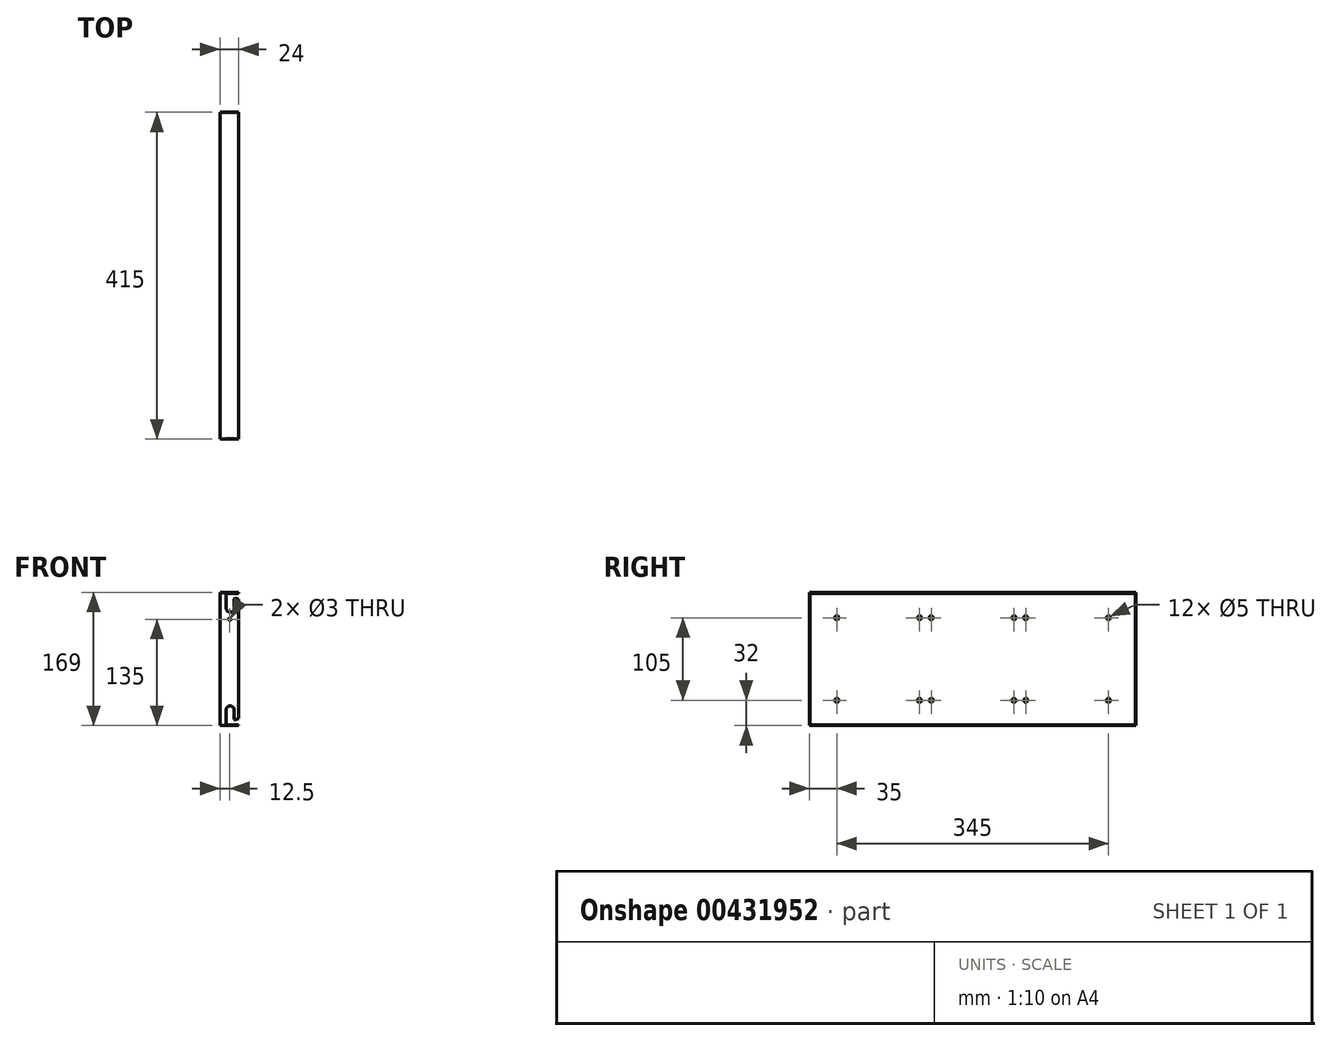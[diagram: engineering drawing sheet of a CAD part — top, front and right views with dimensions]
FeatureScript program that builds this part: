
annotation { "Feature Type Name" : "Feature", "Feature Type Description" : "" }
export const myFeature = defineFeature(function(context is Context, id is Id, definition is map)
    precondition{}
    {
        {
            var Q0;
            Q0=qCreatedBy(makeId("Right.planeOp"),FACE);
            var sketch = newSketch(context, id + "F0", { "sketchPlane" : qUnion([Q0])});
            skLineSegment(sketch, "E0.bottom", {"start": v(-207.5, 84.5) * mm, "end": v(207.5, 84.5) * mm});
            skLineSegment(sketch, "E0.top", {"start": v(-207.5, -84.5) * mm, "end": v(207.5, -84.5) * mm});
            skLineSegment(sketch, "E0.left", {"start": v(-207.5, 84.5) * mm, "end": v(-207.5, -84.5) * mm});
            skLineSegment(sketch, "E0.right", {"start": v(207.5, 84.5) * mm, "end": v(207.5, -84.5) * mm});
            skPoint(sketch, "E0.middle", {"position": v(0, 0) * mm});
            skSolve(sketch);
        }
        {
            var Q0;
            Q0 = qSketchRegion(id + "F0", true);
            extrude(context, id + "F1", {"entities" : qUnion([Q0]), "depth" : 24 * mm});
        }
        {
            var Q0;
            Q0=makeQuery(id+"F1.opExtrude","CAP_FACE",FACE,{"disambiguationData":[OSD([sQuery(id+"F0.wireOp",EDGE,"E0.bottom"),sQuery(id+"F0.wireOp",EDGE,"E0.top"),sQuery(id+"F0.wireOp",EDGE,"E0.left"),sQuery(id+"F0.wireOp",EDGE,"E0.right")])],"isStart":false});
            var sketch = newSketch(context, id + "F2", { "sketchPlane" : qUnion([Q0])});
            skLineSegment(sketch, "E1.bottom", {"start": v(-206.5, 83.5) * mm, "end": v(206.5, 83.5) * mm});
            skLineSegment(sketch, "E1.top", {"start": v(-206.5, -83.5) * mm, "end": v(206.5, -83.5) * mm});
            skLineSegment(sketch, "E1.left", {"start": v(-206.5, 83.5) * mm, "end": v(-206.5, -83.5) * mm});
            skLineSegment(sketch, "E1.right", {"start": v(206.5, 83.5) * mm, "end": v(206.5, -83.5) * mm});
            skPoint(sketch, "E1.middle", {"position": v(0, 0) * mm});
            skSolve(sketch);
        }
        {
            var Q0;
            Q0 = qSketchRegion(id + "F2", true);
            extrude(context, id + "F3", {"entities" : qUnion([Q0]), "operationType" : NewBodyOperationType.REMOVE, "oppositeDirection" : true, "depth" : 23 * mm});
        }
        {
            var Q0;
            Q0=makeQuery(id+"F1.opExtrude","SWEPT_FACE",FACE,{"disambiguationData":[OSD([sQuery(id+"F0.wireOp",EDGE,"E0.left")])]});
            var sketch = newSketch(context, id + "F4", { "sketchPlane" : qUnion([Q0])});
            skLineSegment(sketch, "E2", {"start": v(24, -83.5) * mm, "end": v(8, -83.5) * mm});
            skLineSegment(sketch, "E3", {"start": v(8, -83.5) * mm, "end": v(8, -64.5) * mm});
            skLineSegment(sketch, "E4", {"start": v(18, -76.5) * mm, "end": v(18, -64.5) * mm});
            skLineSegment(sketch, "E5", {"start": v(18, -64.5) * mm, "end": v(8, -64.5) * mm, "construction": true});
            skArc(sketch, "E6", {"start": v(8, -64.5) * mm, "mid": v(13, -59.5) * mm, "end": v(18, -64.5) * mm});
            skLineSegment(sketch, "E7", {"start": v(18, -76.5) * mm, "end": v(19.5, -77.5) * mm});
            skLineSegment(sketch, "E8", {"start": v(24, -75.5) * mm, "end": v(24, -83.5) * mm});
            skLineSegment(sketch, "E9", {"start": v(19.5, -77.5) * mm, "end": v(24, -75.5) * mm});
            skLineSegment(sketch, "E10", {"start": v(0, 0) * mm, "end": v(24, 0) * mm, "construction": true});
            skLineSegment(sketch, "E11.MirrorCS", {"start": v(18, 76.5) * mm, "end": v(19.5, 77.5) * mm});
            skLineSegment(sketch, "E12.MirrorCS", {"start": v(24, 75.5) * mm, "end": v(24, 83.5) * mm});
            skLineSegment(sketch, "E13.MirrorCS", {"start": v(19.5, 77.5) * mm, "end": v(24, 75.5) * mm});
            skLineSegment(sketch, "E14.MirrorCS", {"start": v(18, 64.5) * mm, "end": v(8, 64.5) * mm, "construction": true});
            skLineSegment(sketch, "E15.MirrorCS", {"start": v(18, 76.5) * mm, "end": v(18, 64.5) * mm});
            skArc(sketch, "E16.MirrorCS", {"start": v(8, 64.5) * mm, "mid": v(13, 59.5) * mm, "end": v(18, 64.5) * mm});
            skLineSegment(sketch, "E17.MirrorCS", {"start": v(24, 83.5) * mm, "end": v(8, 83.5) * mm});
            skLineSegment(sketch, "E18.MirrorCS", {"start": v(8, 83.5) * mm, "end": v(8, 64.5) * mm});
            skSolve(sketch);
        }
        {
            var Q0;
            Q0 = qSketchRegion(id + "F4", true);
            extrude(context, id + "F5", {"entities" : qUnion([Q0]), "operationType" : NewBodyOperationType.REMOVE, "endBound" : BoundingType.THROUGH_ALL, "oppositeDirection" : true, "depth" : 25 * mm});
        }
        {
            var Q0;
            Q0=makeQuery(id+"F1.opExtrude","SWEPT_FACE",FACE,{"disambiguationData":[OSD([sQuery(id+"F0.wireOp",EDGE,"E0.left")])]});
            var sketch = newSketch(context, id + "F6", { "sketchPlane" : qUnion([Q0])});
            skCircle(sketch, "E19", {"center": v(12.5, 50.5) * mm, "radius": 1.5 * mm});
            skSolve(sketch);
        }
        {
            var Q0;
            Q0 = qSketchRegion(id + "F6", true);
            extrude(context, id + "F7", {"entities" : qUnion([Q0]), "operationType" : NewBodyOperationType.REMOVE, "endBound" : BoundingType.THROUGH_ALL, "oppositeDirection" : true, "depth" : 25 * mm});
        }
        {
            var Q0;
            Q0=makeQuery(id+"F1.opExtrude","CAP_FACE",FACE,{"disambiguationData":[OSD([sQuery(id+"F0.wireOp",EDGE,"E0.bottom"),sQuery(id+"F0.wireOp",EDGE,"E0.top"),sQuery(id+"F0.wireOp",EDGE,"E0.left"),sQuery(id+"F0.wireOp",EDGE,"E0.right")])],"isStart":true});
            var sketch = newSketch(context, id + "F8", { "sketchPlane" : qUnion([Q0])});
            skCircle(sketch, "E20", {"center": v(-172.5, 52.5) * mm, "radius": 2.5 * mm});
            skCircle(sketch, "E21", {"center": v(-67.5, 52.5) * mm, "radius": 2.5 * mm});
            skCircle(sketch, "E22", {"center": v(-52.5, 52.5) * mm, "radius": 2.5 * mm});
            skLineSegment(sketch, "E23", {"start": v(0, 0) * mm, "end": v(-207.5, 0) * mm, "construction": true});
            skCircle(sketch, "E24.MirrorC", {"center": v(-67.5, -52.5) * mm, "radius": 2.5 * mm});
            skCircle(sketch, "E25.MirrorC", {"center": v(-172.5, -52.5) * mm, "radius": 2.5 * mm});
            skCircle(sketch, "E26.MirrorC", {"center": v(-52.5, -52.5) * mm, "radius": 2.5 * mm});
            skLineSegment(sketch, "E27", {"start": v(0, 84.5) * mm, "end": v(0, -84.5) * mm, "construction": true});
            skCircle(sketch, "E28.MirrorC", {"center": v(67.5, -52.5) * mm, "radius": 2.5 * mm});
            skCircle(sketch, "E29.MirrorC", {"center": v(52.5, 52.5) * mm, "radius": 2.5 * mm});
            skCircle(sketch, "E30.MirrorC", {"center": v(67.5, 52.5) * mm, "radius": 2.5 * mm});
            skCircle(sketch, "E31.MirrorC", {"center": v(172.5, 52.5) * mm, "radius": 2.5 * mm});
            skCircle(sketch, "E32.MirrorC", {"center": v(172.5, -52.5) * mm, "radius": 2.5 * mm});
            skCircle(sketch, "E33.MirrorC", {"center": v(52.5, -52.5) * mm, "radius": 2.5 * mm});
            skSolve(sketch);
        }
        {
            var Q0;
            Q0 = qSketchRegion(id + "F8", true);
            extrude(context, id + "F9", {"entities" : qUnion([Q0]), "operationType" : NewBodyOperationType.REMOVE, "endBound" : BoundingType.UP_TO_NEXT, "oppositeDirection" : true, "depth" : 25 * mm});
        }
    });
